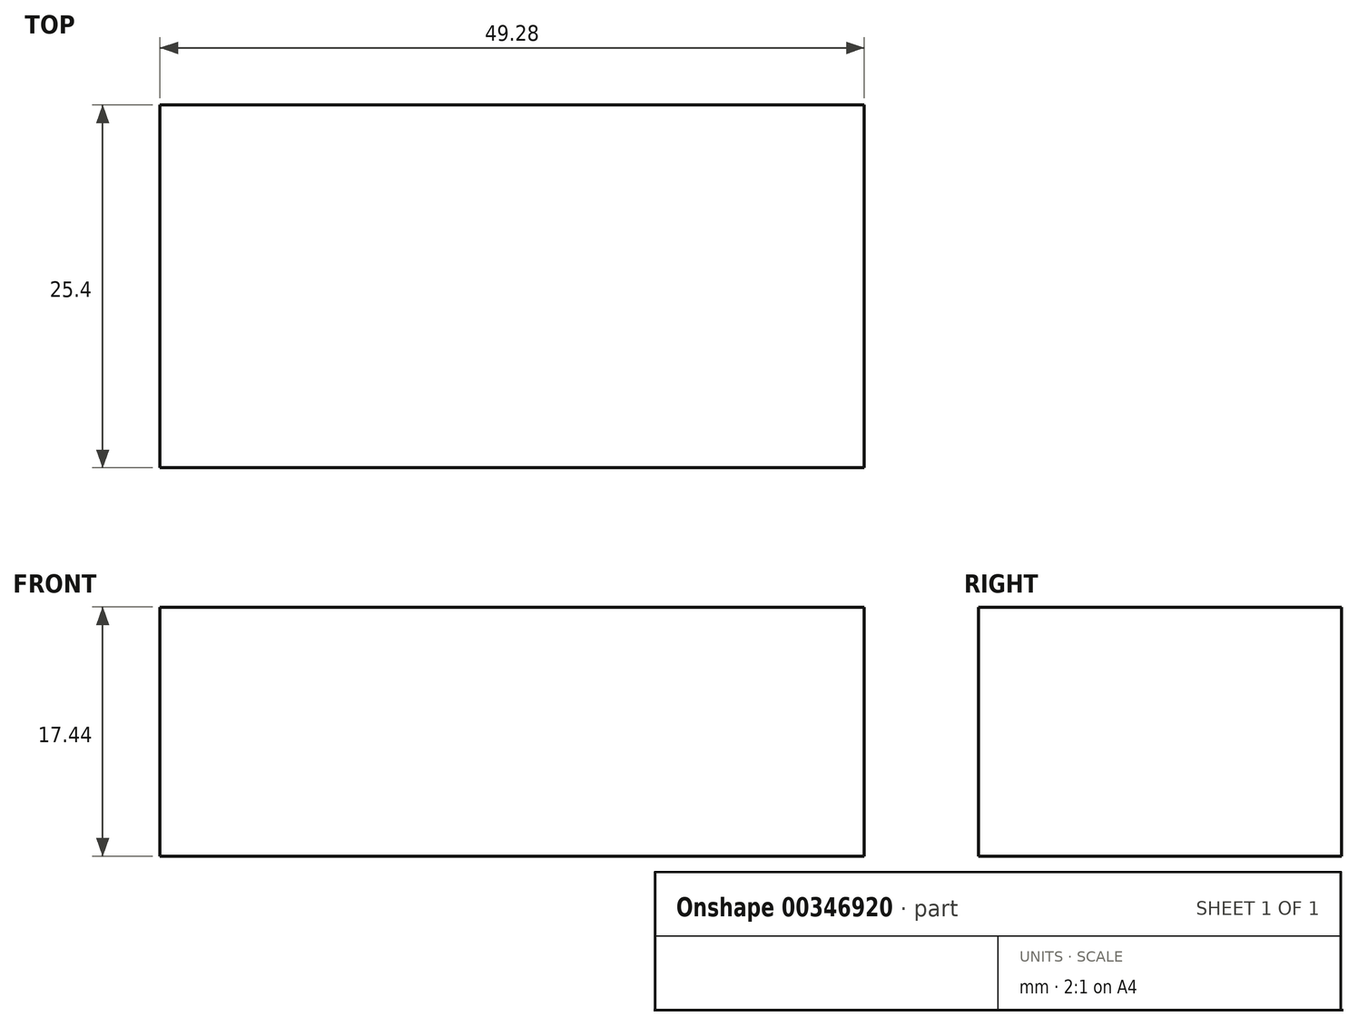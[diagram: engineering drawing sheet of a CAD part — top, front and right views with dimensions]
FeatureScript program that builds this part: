
annotation { "Feature Type Name" : "Feature", "Feature Type Description" : "" }
export const myFeature = defineFeature(function(context is Context, id is Id, definition is map)
    precondition{}
    {
        {
            var Q0;
            Q0=qCreatedBy(makeId("Front.planeOp"),FACE);
            var sketch = newSketch(context, id + "F0", { "sketchPlane" : qUnion([Q0])});
            skLineSegment(sketch, "E0.bottom", {"start": v(24.64, -8.72) * mm, "end": v(-24.64, -8.72) * mm});
            skLineSegment(sketch, "E0.top", {"start": v(24.64, 8.72) * mm, "end": v(-24.64, 8.72) * mm});
            skLineSegment(sketch, "E0.left", {"start": v(24.64, -8.72) * mm, "end": v(24.64, 8.72) * mm});
            skLineSegment(sketch, "E0.right", {"start": v(-24.64, -8.72) * mm, "end": v(-24.64, 8.72) * mm});
            skPoint(sketch, "E0.middle", {"position": v(0, 0) * mm});
            skSolve(sketch);
        }
        {
            var Q0;
            Q0=makeQuery(id+"F0.imprint","IMPRINT",FACE,{"disambiguationData":[TD([[makeQuery(id+"F0.imprint","IMPRINT",EDGE,{"derivedFrom":sQuery(id+"F0.wireOp",EDGE,"E0.bottom")}),-1.0]])]});
            extrude(context, id + "F1", {"entities" : qUnion([Q0]), "endBound" : BoundingType.SYMMETRIC, "depth" : 25.4 * mm});
        }
    });
